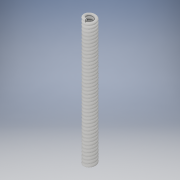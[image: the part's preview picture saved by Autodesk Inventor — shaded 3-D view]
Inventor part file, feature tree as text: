
AUTODESK INVENTOR PART (.ipt)
format: ipt  version: 2018 (Build 220112000, 112)  size: 1,000,448 bytes
history: native  units: in
note: dims shown in document units (in); Inventor stores cm internally (conversion verified against a paired STEP export)
features: helix x1, sketch x1
ambient origin geometry x8: Origin, YZ Plane, XZ Plane, XY Plane, X Axis, Y Axis, Z Axis, Center Point
bodies: Solid1 (feature_tree)
feature tree (2):
  helix  "Coil1"  [1 undecoded]
  sketch  "Sketch1"  dims[d1=0.044in d2=1.0in d3=0.9151in d4=15.748in d5=0.0in d6=0.3436in d7=0.0in d8=0.3436in d9=0.0in]
note: 1 required parameter value undecoded (feature->parameter linkage not recoverable at this tier; creation-order binding heuristic only, values carry confidence <= 0.55)
